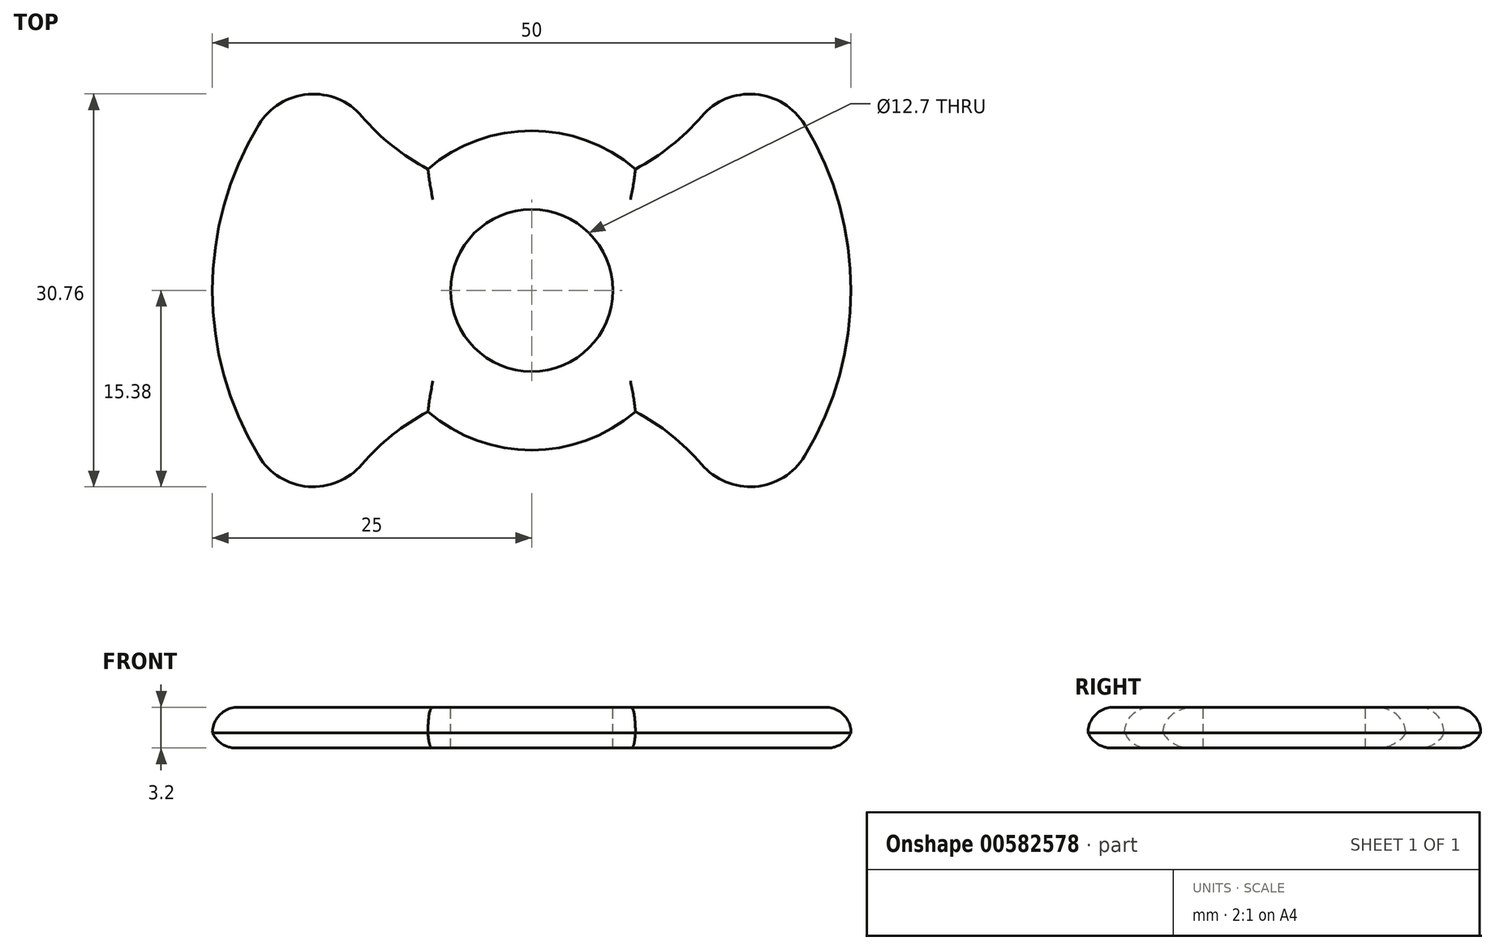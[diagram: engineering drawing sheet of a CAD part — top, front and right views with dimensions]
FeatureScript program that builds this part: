
annotation { "Feature Type Name" : "Feature", "Feature Type Description" : "" }
export const myFeature = defineFeature(function(context is Context, id is Id, definition is map)
    precondition{}
    {
        {
            var Q0;
            Q0=qCreatedBy(makeId("Top.planeOp"),FACE);
            var sketch = newSketch(context, id + "F0", { "sketchPlane" : qUnion([Q0])});
            skArc(sketch, "E0", {"start": v(16.4, -18.88) * mm, "mid": v(25, 0) * mm, "end": v(16.4, 18.88) * mm});
            skArc(sketch, "E1", {"start": v(-16.4, 18.88) * mm, "mid": v(0, 7.5) * mm, "end": v(16.4, 18.88) * mm});
            skArc(sketch, "E2", {"start": v(16.4, -18.88) * mm, "mid": v(0, -7.5) * mm, "end": v(-16.4, -18.88) * mm});
            skArc(sketch, "E3.trimOffspring", {"start": v(-16.4, 18.88) * mm, "mid": v(-25, 0) * mm, "end": v(-16.4, -18.88) * mm});
            skCircle(sketch, "E4", {"center": v(0, 0) * mm, "radius": 6.35 * mm});
            skCircle(sketch, "E5", {"center": v(0, 0) * mm, "radius": 12.5 * mm});
            skSolve(sketch);
        }
        {
            var Q0;
            {var subQ0=sQuery(id+"F0.wireOp",EDGE,"E3.trimOffspring");Q0=makeQuery(id+"F0.imprint","IMPRINT",FACE,{"disambiguationData":[TD([[makeQuery(id+"F0.imprint","IMPRINT",EDGE,{"derivedFrom":subQ0}),1.0]])]});}
            var Q1;
            Q1=makeQuery(id+"F0.imprint","IMPRINT",FACE,{"disambiguationData":[TD([[makeQuery(id+"F0.imprint","IMPRINT",EDGE,{"derivedFrom":sQuery(id+"F0.wireOp",EDGE,"E4")}),-1.0]])]});
            var Q2;
            {var subQ0=sQuery(id+"F0.wireOp",EDGE,"E0");Q2=makeQuery(id+"F0.imprint","IMPRINT",FACE,{"disambiguationData":[TD([[makeQuery(id+"F0.imprint","IMPRINT",EDGE,{"derivedFrom":subQ0}),1.0]])]});}
            var Q3;
            {var subQ0=sQuery(id+"F0.wireOp",EDGE,"E5");var subQ1=sQuery(id+"F0.wireOp",EDGE,"E2");var subQ2=makeQuery(id+"F0.imprint","INTERSECT",VERTEX,{"disambiguationData":[OD(0.0)],"derivedFrom":[subQ1,subQ0]});Q3=makeQuery(id+"F0.imprint","IMPRINT",FACE,{"disambiguationData":[TD([[makeQuery(id+"F0.imprint","IMPRINT",EDGE,{"disambiguationData":[TD([[subQ2,-1.0]])],"derivedFrom":subQ1}),1.0]])]});}
            var Q4;
            {var subQ0=sQuery(id+"F0.wireOp",EDGE,"E5");var subQ1=sQuery(id+"F0.wireOp",EDGE,"E1");var subQ2=makeQuery(id+"F0.imprint","INTERSECT",VERTEX,{"disambiguationData":[OD(0.0)],"derivedFrom":[subQ1,subQ0]});Q4=makeQuery(id+"F0.imprint","IMPRINT",FACE,{"disambiguationData":[TD([[makeQuery(id+"F0.imprint","IMPRINT",EDGE,{"disambiguationData":[TD([[subQ2,-1.0]])],"derivedFrom":subQ1}),1.0]])]});}
            extrude(context, id + "F1", {"entities" : qUnion([Q0, Q1, Q2, Q3, Q4]), "oppositeDirection" : true, "depth" : 1.6 * mm, "offsetDistance" : 25 * mm});
        }
        {
            var Q0;
            Q0=makeQuery(id+"F1.opExtrude","CAP_FACE",FACE,{"disambiguationData":[OSD([sQuery(id+"F0.wireOp",EDGE,"E0"),sQuery(id+"F0.wireOp",EDGE,"E1"),sQuery(id+"F0.wireOp",EDGE,"E2"),sQuery(id+"F0.wireOp",EDGE,"E3.trimOffspring"),sQuery(id+"F0.wireOp",EDGE,"E4"),sQuery(id+"F0.wireOp",EDGE,"E5")])],"isStart":true});
            extrude(context, id + "F2", {"entities" : qUnion([Q0]), "operationType" : NewBodyOperationType.ADD, "depth" : 1.6 * mm, "offsetDistance" : 25 * mm});
        }
        {
            var Q0;
            Q0=makeQuery(id+"F2.opExtrude","CAP_EDGE",EDGE,{"disambiguationData":[OSD([sQuery(id+"F0.wireOp",EDGE,"E0")])],"isStart":false});
            var Q1;
            {var subQ0=sQuery(id+"F0.wireOp",EDGE,"E1");Q1=makeQuery(id+"F2.opExtrude","CAP_EDGE",EDGE,{"disambiguationData":[OSD([subQ0]),TDD([makeQuery(id+"F1.opExtrude","CAP_EDGE",EDGE,{"disambiguationData":[OSD([subQ0]),TDD([makeQuery(id+"F0.imprint","IMPRINT",EDGE,{"disambiguationData":[TD([[makeQuery(id+"F0.imprint","INTERSECT",VERTEX,{"derivedFrom":[sQuery(id+"F0.wireOp",EDGE,"E0"),subQ0]}),1.0]])],"derivedFrom":subQ0})])],"isStart":true})])],"isStart":false});}
            var Q2;
            {var subQ0=sQuery(id+"F0.wireOp",EDGE,"E5");var subQ1=sQuery(id+"F0.wireOp",EDGE,"E1");Q2=makeQuery(id+"F2.opExtrude","CAP_EDGE",EDGE,{"disambiguationData":[OSD([subQ0]),TDD([makeQuery(id+"F1.opExtrude","CAP_EDGE",EDGE,{"disambiguationData":[OSD([subQ0]),TDD([makeQuery(id+"F0.imprint","IMPRINT",EDGE,{"disambiguationData":[TD([[makeQuery(id+"F0.imprint","INTERSECT",VERTEX,{"disambiguationData":[OD(0.0)],"derivedFrom":[subQ1,subQ0]}),1.0]])],"derivedFrom":subQ0})])],"isStart":true})])],"isStart":false});}
            var Q3;
            {var subQ0=sQuery(id+"F0.wireOp",EDGE,"E1");Q3=makeQuery(id+"F2.opExtrude","CAP_EDGE",EDGE,{"disambiguationData":[OSD([subQ0]),TDD([makeQuery(id+"F1.opExtrude","CAP_EDGE",EDGE,{"disambiguationData":[OSD([subQ0]),TDD([makeQuery(id+"F0.imprint","IMPRINT",EDGE,{"disambiguationData":[TD([[makeQuery(id+"F0.imprint","INTERSECT",VERTEX,{"derivedFrom":[subQ0,sQuery(id+"F0.wireOp",EDGE,"E3.trimOffspring")]}),-1.0]])],"derivedFrom":subQ0})])],"isStart":true})])],"isStart":false});}
            var Q4;
            Q4=makeQuery(id+"F2.opExtrude","CAP_EDGE",EDGE,{"disambiguationData":[OSD([sQuery(id+"F0.wireOp",EDGE,"E3.trimOffspring")])],"isStart":false});
            var Q5;
            {var subQ0=sQuery(id+"F0.wireOp",EDGE,"E2");Q5=makeQuery(id+"F2.opExtrude","CAP_EDGE",EDGE,{"disambiguationData":[OSD([subQ0]),TDD([makeQuery(id+"F1.opExtrude","CAP_EDGE",EDGE,{"disambiguationData":[OSD([subQ0]),TDD([makeQuery(id+"F0.imprint","IMPRINT",EDGE,{"disambiguationData":[TD([[makeQuery(id+"F0.imprint","INTERSECT",VERTEX,{"derivedFrom":[subQ0,sQuery(id+"F0.wireOp",EDGE,"E3.trimOffspring")]}),1.0]])],"derivedFrom":subQ0})])],"isStart":true})])],"isStart":false});}
            var Q6;
            {var subQ0=sQuery(id+"F0.wireOp",EDGE,"E5");var subQ1=sQuery(id+"F0.wireOp",EDGE,"E2");Q6=makeQuery(id+"F2.opExtrude","CAP_EDGE",EDGE,{"disambiguationData":[OSD([subQ0]),TDD([makeQuery(id+"F1.opExtrude","CAP_EDGE",EDGE,{"disambiguationData":[OSD([subQ0]),TDD([makeQuery(id+"F0.imprint","IMPRINT",EDGE,{"disambiguationData":[TD([[makeQuery(id+"F0.imprint","INTERSECT",VERTEX,{"disambiguationData":[OD(0.0)],"derivedFrom":[subQ1,subQ0]}),1.0]])],"derivedFrom":subQ0})])],"isStart":true})])],"isStart":false});}
            var Q7;
            {var subQ0=sQuery(id+"F0.wireOp",EDGE,"E2");Q7=makeQuery(id+"F2.opExtrude","CAP_EDGE",EDGE,{"disambiguationData":[OSD([subQ0]),TDD([makeQuery(id+"F1.opExtrude","CAP_EDGE",EDGE,{"disambiguationData":[OSD([subQ0]),TDD([makeQuery(id+"F0.imprint","IMPRINT",EDGE,{"disambiguationData":[TD([[makeQuery(id+"F0.imprint","INTERSECT",VERTEX,{"derivedFrom":[sQuery(id+"F0.wireOp",EDGE,"E0"),subQ0]}),-1.0]])],"derivedFrom":subQ0})])],"isStart":true})])],"isStart":false});}
            fillet(context, id + "F3", {"entities" : qUnion([Q0, Q1, Q2, Q3, Q4, Q5, Q6, Q7]), "radius" : 2 * mm, "tangentPropagation" : true, "allowEdgeOverflow" : false});
        }
        {
            var Q0;
            {var subQ0=sQuery(id+"F0.wireOp",EDGE,"E1");var subQ1=sQuery(id+"F0.wireOp",EDGE,"E0");Q0=makeQuery(id+"F3.opFillet","BLEND_EDGE",EDGE,{"blendedFrom":[makeQuery(id+"F2.opExtrude","CAP_EDGE",EDGE,{"disambiguationData":[OSD([subQ1])],"isStart":false}),makeQuery(id+"F2.opExtrude","CAP_EDGE",EDGE,{"disambiguationData":[OSD([subQ0]),TDD([makeQuery(id+"F1.opExtrude","CAP_EDGE",EDGE,{"disambiguationData":[OSD([subQ0]),TDD([makeQuery(id+"F0.imprint","IMPRINT",EDGE,{"disambiguationData":[TD([[makeQuery(id+"F0.imprint","INTERSECT",VERTEX,{"derivedFrom":[subQ1,subQ0]}),1.0]])],"derivedFrom":subQ0})])],"isStart":true})])],"isStart":false})],"blendedInto":[]});}
            fillet(context, id + "F4", {"entities" : qUnion([Q0]), "radius" : 5 * mm, "tangentPropagation" : true, "allowEdgeOverflow" : false});
        }
        {
            var Q0;
            {var subQ0=sQuery(id+"F0.wireOp",EDGE,"E2");var subQ1=sQuery(id+"F0.wireOp",EDGE,"E0");Q0=makeQuery(id+"F3.opFillet","BLEND_EDGE",EDGE,{"blendedFrom":[makeQuery(id+"F2.opExtrude","CAP_EDGE",EDGE,{"disambiguationData":[OSD([subQ1])],"isStart":false}),makeQuery(id+"F2.opExtrude","CAP_EDGE",EDGE,{"disambiguationData":[OSD([subQ0]),TDD([makeQuery(id+"F1.opExtrude","CAP_EDGE",EDGE,{"disambiguationData":[OSD([subQ0]),TDD([makeQuery(id+"F0.imprint","IMPRINT",EDGE,{"disambiguationData":[TD([[makeQuery(id+"F0.imprint","INTERSECT",VERTEX,{"derivedFrom":[subQ1,subQ0]}),-1.0]])],"derivedFrom":subQ0})])],"isStart":true})])],"isStart":false})],"blendedInto":[]});}
            fillet(context, id + "F5", {"entities" : qUnion([Q0]), "radius" : 5 * mm, "tangentPropagation" : true, "allowEdgeOverflow" : false});
        }
        {
            var Q0;
            Q0=makeQuery(id+"F2.opExtrude","CAP_FACE",FACE,{"disambiguationData":[OSD([sQuery(id+"F0.wireOp",EDGE,"E0"),sQuery(id+"F0.wireOp",EDGE,"E1"),sQuery(id+"F0.wireOp",EDGE,"E2"),sQuery(id+"F0.wireOp",EDGE,"E3.trimOffspring"),sQuery(id+"F0.wireOp",EDGE,"E4"),sQuery(id+"F0.wireOp",EDGE,"E5")])],"isStart":false});
            var sketch = newSketch(context, id + "F6", { "sketchPlane" : qUnion([Q0])});
            skSolve(sketch);
        }
        {
            var Q0;
            {var subQ0=sQuery(id+"F0.wireOp",EDGE,"E3.trimOffspring");var subQ1=sQuery(id+"F0.wireOp",EDGE,"E2");Q0=makeQuery(id+"F3.opFillet","BLEND_EDGE",EDGE,{"blendedFrom":[makeQuery(id+"F2.opExtrude","CAP_EDGE",EDGE,{"disambiguationData":[OSD([subQ1]),TDD([makeQuery(id+"F1.opExtrude","CAP_EDGE",EDGE,{"disambiguationData":[OSD([subQ1]),TDD([makeQuery(id+"F0.imprint","IMPRINT",EDGE,{"disambiguationData":[TD([[makeQuery(id+"F0.imprint","INTERSECT",VERTEX,{"derivedFrom":[subQ1,subQ0]}),1.0]])],"derivedFrom":subQ1})])],"isStart":true})])],"isStart":false}),makeQuery(id+"F2.opExtrude","CAP_EDGE",EDGE,{"disambiguationData":[OSD([subQ0])],"isStart":false})],"blendedInto":[]});}
            fillet(context, id + "F7", {"entities" : qUnion([Q0]), "radius" : 5 * mm, "tangentPropagation" : true, "allowEdgeOverflow" : false});
        }
        {
            var Q0;
            {var subQ0=sQuery(id+"F0.wireOp",EDGE,"E3.trimOffspring");var subQ1=sQuery(id+"F0.wireOp",EDGE,"E1");Q0=makeQuery(id+"F3.opFillet","BLEND_EDGE",EDGE,{"blendedFrom":[makeQuery(id+"F2.opExtrude","CAP_EDGE",EDGE,{"disambiguationData":[OSD([subQ1]),TDD([makeQuery(id+"F1.opExtrude","CAP_EDGE",EDGE,{"disambiguationData":[OSD([subQ1]),TDD([makeQuery(id+"F0.imprint","IMPRINT",EDGE,{"disambiguationData":[TD([[makeQuery(id+"F0.imprint","INTERSECT",VERTEX,{"derivedFrom":[subQ1,subQ0]}),-1.0]])],"derivedFrom":subQ1})])],"isStart":true})])],"isStart":false}),makeQuery(id+"F2.opExtrude","CAP_EDGE",EDGE,{"disambiguationData":[OSD([subQ0])],"isStart":false})],"blendedInto":[]});}
            fillet(context, id + "F8", {"entities" : qUnion([Q0]), "radius" : 5 * mm, "tangentPropagation" : true, "allowEdgeOverflow" : false});
        }
        {
            var Q0;
            Q0=makeQuery(id+"F1.opExtrude","CAP_EDGE",EDGE,{"disambiguationData":[OSD([sQuery(id+"F0.wireOp",EDGE,"E0")])],"isStart":false});
            var Q1;
            {var subQ0=sQuery(id+"F0.wireOp",EDGE,"E2");var subQ1=sQuery(id+"F0.wireOp",EDGE,"E0");Q1=makeQuery(id+"F5.opFillet","BLEND_EDGE",EDGE,{"blendedFrom":[makeQuery(id+"F2.boolean.opBoolean","MERGE",EDGE,{"derivedFrom":[makeQuery(id+"F1.opExtrude","SWEPT_EDGE",EDGE,{"disambiguationData":[OSD([subQ1,subQ0])]}),makeQuery(id+"F2.opExtrude","SWEPT_EDGE",EDGE,{"disambiguationData":[OSD([subQ1,subQ0])]})]}),makeQuery(id+"F1.opExtrude","CAP_FACE",FACE,{"disambiguationData":[OSD([subQ1,sQuery(id+"F0.wireOp",EDGE,"E1"),subQ0,sQuery(id+"F0.wireOp",EDGE,"E3.trimOffspring"),sQuery(id+"F0.wireOp",EDGE,"E4"),sQuery(id+"F0.wireOp",EDGE,"E5")])],"isStart":false})],"blendedInto":[makeQuery(id+"F1.opExtrude","CAP_FACE",FACE,{"disambiguationData":[OSD([subQ1,sQuery(id+"F0.wireOp",EDGE,"E1"),subQ0,sQuery(id+"F0.wireOp",EDGE,"E3.trimOffspring"),sQuery(id+"F0.wireOp",EDGE,"E4"),sQuery(id+"F0.wireOp",EDGE,"E5")])],"isStart":false})]});}
            var Q2;
            {var subQ0=sQuery(id+"F0.wireOp",EDGE,"E2");Q2=makeQuery(id+"F1.opExtrude","CAP_EDGE",EDGE,{"disambiguationData":[OSD([subQ0]),TDD([makeQuery(id+"F0.imprint","IMPRINT",EDGE,{"disambiguationData":[TD([[makeQuery(id+"F0.imprint","INTERSECT",VERTEX,{"derivedFrom":[sQuery(id+"F0.wireOp",EDGE,"E0"),subQ0]}),-1.0]])],"derivedFrom":subQ0})])],"isStart":false});}
            var Q3;
            {var subQ0=sQuery(id+"F0.wireOp",EDGE,"E5");var subQ1=sQuery(id+"F0.wireOp",EDGE,"E2");Q3=makeQuery(id+"F1.opExtrude","CAP_EDGE",EDGE,{"disambiguationData":[OSD([subQ0]),TDD([makeQuery(id+"F0.imprint","IMPRINT",EDGE,{"disambiguationData":[TD([[makeQuery(id+"F0.imprint","INTERSECT",VERTEX,{"disambiguationData":[OD(0.0)],"derivedFrom":[subQ1,subQ0]}),1.0]])],"derivedFrom":subQ0})])],"isStart":false});}
            var Q4;
            {var subQ0=sQuery(id+"F0.wireOp",EDGE,"E2");Q4=makeQuery(id+"F1.opExtrude","CAP_EDGE",EDGE,{"disambiguationData":[OSD([subQ0]),TDD([makeQuery(id+"F0.imprint","IMPRINT",EDGE,{"disambiguationData":[TD([[makeQuery(id+"F0.imprint","INTERSECT",VERTEX,{"derivedFrom":[subQ0,sQuery(id+"F0.wireOp",EDGE,"E3.trimOffspring")]}),1.0]])],"derivedFrom":subQ0})])],"isStart":false});}
            var Q5;
            {var subQ0=sQuery(id+"F0.wireOp",EDGE,"E3.trimOffspring");var subQ1=sQuery(id+"F0.wireOp",EDGE,"E2");Q5=makeQuery(id+"F7.opFillet","BLEND_EDGE",EDGE,{"blendedFrom":[makeQuery(id+"F2.boolean.opBoolean","MERGE",EDGE,{"derivedFrom":[makeQuery(id+"F1.opExtrude","SWEPT_EDGE",EDGE,{"disambiguationData":[OSD([subQ1,subQ0])]}),makeQuery(id+"F2.opExtrude","SWEPT_EDGE",EDGE,{"disambiguationData":[OSD([subQ1,subQ0])]})]}),makeQuery(id+"F1.opExtrude","CAP_FACE",FACE,{"disambiguationData":[OSD([sQuery(id+"F0.wireOp",EDGE,"E0"),sQuery(id+"F0.wireOp",EDGE,"E1"),subQ1,subQ0,sQuery(id+"F0.wireOp",EDGE,"E4"),sQuery(id+"F0.wireOp",EDGE,"E5")])],"isStart":false})],"blendedInto":[makeQuery(id+"F1.opExtrude","CAP_FACE",FACE,{"disambiguationData":[OSD([sQuery(id+"F0.wireOp",EDGE,"E0"),sQuery(id+"F0.wireOp",EDGE,"E1"),subQ1,subQ0,sQuery(id+"F0.wireOp",EDGE,"E4"),sQuery(id+"F0.wireOp",EDGE,"E5")])],"isStart":false})]});}
            var Q6;
            Q6=makeQuery(id+"F1.opExtrude","CAP_EDGE",EDGE,{"disambiguationData":[OSD([sQuery(id+"F0.wireOp",EDGE,"E3.trimOffspring")])],"isStart":false});
            var Q7;
            {var subQ0=sQuery(id+"F0.wireOp",EDGE,"E3.trimOffspring");var subQ1=sQuery(id+"F0.wireOp",EDGE,"E1");Q7=makeQuery(id+"F8.opFillet","BLEND_EDGE",EDGE,{"blendedFrom":[makeQuery(id+"F2.boolean.opBoolean","MERGE",EDGE,{"derivedFrom":[makeQuery(id+"F1.opExtrude","SWEPT_EDGE",EDGE,{"disambiguationData":[OSD([subQ1,subQ0])]}),makeQuery(id+"F2.opExtrude","SWEPT_EDGE",EDGE,{"disambiguationData":[OSD([subQ1,subQ0])]})]}),makeQuery(id+"F1.opExtrude","CAP_FACE",FACE,{"disambiguationData":[OSD([sQuery(id+"F0.wireOp",EDGE,"E0"),subQ1,sQuery(id+"F0.wireOp",EDGE,"E2"),subQ0,sQuery(id+"F0.wireOp",EDGE,"E4"),sQuery(id+"F0.wireOp",EDGE,"E5")])],"isStart":false})],"blendedInto":[makeQuery(id+"F1.opExtrude","CAP_FACE",FACE,{"disambiguationData":[OSD([sQuery(id+"F0.wireOp",EDGE,"E0"),subQ1,sQuery(id+"F0.wireOp",EDGE,"E2"),subQ0,sQuery(id+"F0.wireOp",EDGE,"E4"),sQuery(id+"F0.wireOp",EDGE,"E5")])],"isStart":false})]});}
            var Q8;
            {var subQ0=sQuery(id+"F0.wireOp",EDGE,"E1");Q8=makeQuery(id+"F1.opExtrude","CAP_EDGE",EDGE,{"disambiguationData":[OSD([subQ0]),TDD([makeQuery(id+"F0.imprint","IMPRINT",EDGE,{"disambiguationData":[TD([[makeQuery(id+"F0.imprint","INTERSECT",VERTEX,{"derivedFrom":[subQ0,sQuery(id+"F0.wireOp",EDGE,"E3.trimOffspring")]}),-1.0]])],"derivedFrom":subQ0})])],"isStart":false});}
            var Q9;
            {var subQ0=sQuery(id+"F0.wireOp",EDGE,"E5");var subQ1=sQuery(id+"F0.wireOp",EDGE,"E1");Q9=makeQuery(id+"F1.opExtrude","CAP_EDGE",EDGE,{"disambiguationData":[OSD([subQ0]),TDD([makeQuery(id+"F0.imprint","IMPRINT",EDGE,{"disambiguationData":[TD([[makeQuery(id+"F0.imprint","INTERSECT",VERTEX,{"disambiguationData":[OD(0.0)],"derivedFrom":[subQ1,subQ0]}),1.0]])],"derivedFrom":subQ0})])],"isStart":false});}
            var Q10;
            {var subQ0=sQuery(id+"F0.wireOp",EDGE,"E1");Q10=makeQuery(id+"F1.opExtrude","CAP_EDGE",EDGE,{"disambiguationData":[OSD([subQ0]),TDD([makeQuery(id+"F0.imprint","IMPRINT",EDGE,{"disambiguationData":[TD([[makeQuery(id+"F0.imprint","INTERSECT",VERTEX,{"derivedFrom":[sQuery(id+"F0.wireOp",EDGE,"E0"),subQ0]}),1.0]])],"derivedFrom":subQ0})])],"isStart":false});}
            var Q11;
            {var subQ0=sQuery(id+"F0.wireOp",EDGE,"E1");var subQ1=sQuery(id+"F0.wireOp",EDGE,"E0");Q11=makeQuery(id+"F4.opFillet","BLEND_EDGE",EDGE,{"blendedFrom":[makeQuery(id+"F2.boolean.opBoolean","MERGE",EDGE,{"derivedFrom":[makeQuery(id+"F1.opExtrude","SWEPT_EDGE",EDGE,{"disambiguationData":[OSD([subQ1,subQ0])]}),makeQuery(id+"F2.opExtrude","SWEPT_EDGE",EDGE,{"disambiguationData":[OSD([subQ1,subQ0])]})]}),makeQuery(id+"F1.opExtrude","CAP_FACE",FACE,{"disambiguationData":[OSD([subQ1,subQ0,sQuery(id+"F0.wireOp",EDGE,"E2"),sQuery(id+"F0.wireOp",EDGE,"E3.trimOffspring"),sQuery(id+"F0.wireOp",EDGE,"E4"),sQuery(id+"F0.wireOp",EDGE,"E5")])],"isStart":false})],"blendedInto":[makeQuery(id+"F1.opExtrude","CAP_FACE",FACE,{"disambiguationData":[OSD([subQ1,subQ0,sQuery(id+"F0.wireOp",EDGE,"E2"),sQuery(id+"F0.wireOp",EDGE,"E3.trimOffspring"),sQuery(id+"F0.wireOp",EDGE,"E4"),sQuery(id+"F0.wireOp",EDGE,"E5")])],"isStart":false})]});}
            fillet(context, id + "F9", {"entities" : qUnion([Q0, Q1, Q2, Q3, Q4, Q5, Q6, Q7, Q8, Q9, Q10, Q11]), "radius" : 2 * mm, "tangentPropagation" : true, "allowEdgeOverflow" : false});
        }
    });
